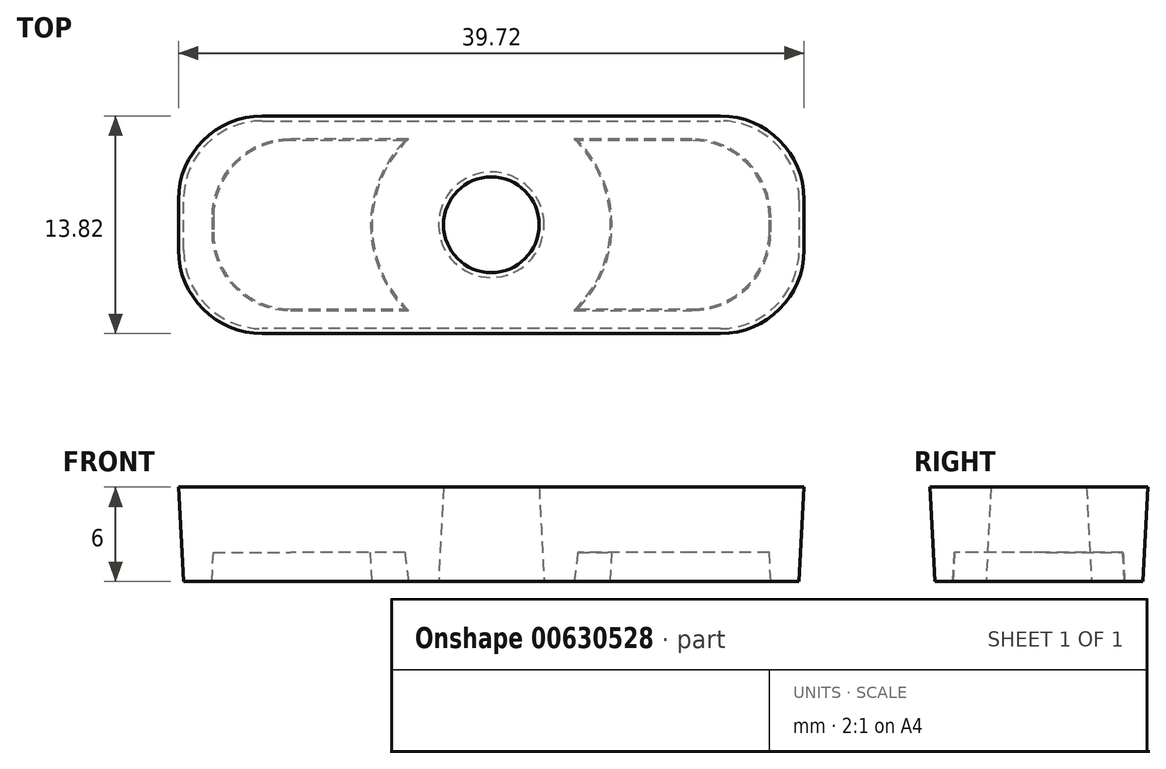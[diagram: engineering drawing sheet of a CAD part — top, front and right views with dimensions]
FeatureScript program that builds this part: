
annotation { "Feature Type Name" : "Feature", "Feature Type Description" : "" }
export const myFeature = defineFeature(function(context is Context, id is Id, definition is map)
    precondition{}
    {
        {
            var Q0;
            Q0=qCreatedBy(makeId("Top.planeOp"),FACE);
            var sketch = newSketch(context, id + "F0", { "sketchPlane" : qUnion([Q0])});
            skLineSegment(sketch, "E0.bottom", {"start": v(-12.75, 5.45) * mm, "end": v(12.75, 5.45) * mm});
            skLineSegment(sketch, "E0.top", {"start": v(-12.75, -5.45) * mm, "end": v(12.75, -5.45) * mm});
            skLineSegment(sketch, "E0.left", {"start": v(-17.75, 0.45) * mm, "end": v(-17.75, -0.45) * mm});
            skLineSegment(sketch, "E0.right", {"start": v(17.75, 0.45) * mm, "end": v(17.75, -0.45) * mm});
            skPoint(sketch, "E0.middle", {"position": v(0, 0) * mm});
            skArc(sketch, "E1", {"start": v(-5.26, 5.45) * mm, "mid": v(-7.58, 0) * mm, "end": v(-5.26, -5.45) * mm});
            skArc(sketch, "E2.trimOffspring", {"start": v(5.26, -5.45) * mm, "mid": v(7.58, 0) * mm, "end": v(5.26, 5.45) * mm});
            skCircle(sketch, "E3", {"center": v(0, 0) * mm, "radius": 3.35 * mm});
            skPoint(sketch, "E4.visualSharp", {"position": v(-17.75, 5.45) * mm});
            skArc(sketch, "E4.filletArc", {"start": v(-12.75, 5.45) * mm, "mid": v(-16.29, 3.99) * mm, "end": v(-17.75, 0.45) * mm});
            skPoint(sketch, "E5.visualSharp", {"position": v(-17.75, -5.45) * mm});
            skArc(sketch, "E5.filletArc", {"start": v(-17.75, -0.45) * mm, "mid": v(-16.29, -3.99) * mm, "end": v(-12.75, -5.45) * mm});
            skPoint(sketch, "E6.visualSharp", {"position": v(17.75, -5.45) * mm});
            skArc(sketch, "E6.filletArc", {"start": v(12.75, -5.45) * mm, "mid": v(16.29, -3.99) * mm, "end": v(17.75, -0.45) * mm});
            skPoint(sketch, "E7.visualSharp", {"position": v(17.75, 5.45) * mm});
            skArc(sketch, "E7.filletArc", {"start": v(17.75, 0.45) * mm, "mid": v(16.29, 3.99) * mm, "end": v(12.75, 5.45) * mm});
            skLineSegment(sketch, "E8.0", {"start": v(-14.55, 6.6) * mm, "end": v(12.75, 6.6) * mm});
            skLineSegment(sketch, "E9.0", {"start": v(-14.55, -6.6) * mm, "end": v(12.75, -6.6) * mm});
            skLineSegment(sketch, "E10.0", {"start": v(-19.55, 1.6) * mm, "end": v(-19.55, -1.6) * mm});
            skPoint(sketch, "E11.visualSharp", {"position": v(-19.55, 6.6) * mm});
            skArc(sketch, "E11.filletArc", {"start": v(-14.55, 6.6) * mm, "mid": v(-18.09, 5.14) * mm, "end": v(-19.55, 1.6) * mm});
            skPoint(sketch, "E12.visualSharp", {"position": v(-19.55, -6.6) * mm});
            skArc(sketch, "E12.filletArc", {"start": v(-19.55, -1.6) * mm, "mid": v(-18.09, -5.14) * mm, "end": v(-14.55, -6.6) * mm});
            skArc(sketch, "E13.MirrorCS", {"start": v(14.55, 6.6) * mm, "mid": v(18.09, 5.14) * mm, "end": v(19.55, 1.6) * mm});
            skLineSegment(sketch, "E14.MirrorCS", {"start": v(19.55, 1.6) * mm, "end": v(19.55, -1.6) * mm});
            skArc(sketch, "E15.MirrorCS", {"start": v(19.55, -1.6) * mm, "mid": v(18.09, -5.14) * mm, "end": v(14.55, -6.6) * mm});
            skLineSegment(sketch, "E16.MirrorCS", {"start": v(14.55, 6.6) * mm, "end": v(-12.75, 6.6) * mm});
            skLineSegment(sketch, "E17.MirrorCS", {"start": v(14.55, -6.6) * mm, "end": v(-12.75, -6.6) * mm});
            skSolve(sketch);
        }
        {
            var Q0;
            Q0=makeQuery(id+"F0.imprint","IMPRINT",FACE,{"disambiguationData":[TD([[makeQuery(id+"F0.imprint","IMPRINT",EDGE,{"derivedFrom":sQuery(id+"F0.wireOp",EDGE,"E0.left")}),-1.0]])]});
            var Q1;
            {var subQ0=sQuery(id+"F0.wireOp",EDGE,"E1");Q1=makeQuery(id+"F0.imprint","IMPRINT",FACE,{"disambiguationData":[TD([[makeQuery(id+"F0.imprint","IMPRINT",EDGE,{"derivedFrom":subQ0}),1.0]])]});}
            extrude(context, id + "F1", {"entities" : qUnion([Q0, Q1]), "depth" : 6 * mm, "offsetDistance" : 25 * mm, "hasDraft" : true, "draftAngle" : 3 * degree});
        }
        {
            var Q0;
            Q0=makeQuery(id+"F1.opExtrude","CAP_FACE",FACE,{"disambiguationData":[OSD([sQuery(id+"F0.wireOp",EDGE,"E0.bottom"),sQuery(id+"F0.wireOp",EDGE,"E0.top"),sQuery(id+"F0.wireOp",EDGE,"E0.left"),sQuery(id+"F0.wireOp",EDGE,"E0.right"),sQuery(id+"F0.wireOp",EDGE,"E1"),sQuery(id+"F0.wireOp",EDGE,"E2.trimOffspring"),sQuery(id+"F0.wireOp",EDGE,"E3"),sQuery(id+"F0.wireOp",EDGE,"E4.filletArc"),sQuery(id+"F0.wireOp",EDGE,"E5.filletArc"),sQuery(id+"F0.wireOp",EDGE,"E6.filletArc"),sQuery(id+"F0.wireOp",EDGE,"E7.filletArc"),sQuery(id+"F0.wireOp",EDGE,"E8.0"),sQuery(id+"F0.wireOp",EDGE,"E9.0"),sQuery(id+"F0.wireOp",EDGE,"E10.0"),sQuery(id+"F0.wireOp",EDGE,"E11.filletArc"),sQuery(id+"F0.wireOp",EDGE,"E12.filletArc"),sQuery(id+"F0.wireOp",EDGE,"E13.MirrorCS"),sQuery(id+"F0.wireOp",EDGE,"E14.MirrorCS"),sQuery(id+"F0.wireOp",EDGE,"E15.MirrorCS"),sQuery(id+"F0.wireOp",EDGE,"E16.MirrorCS"),sQuery(id+"F0.wireOp",EDGE,"E17.MirrorCS")])],"isStart":false});
            var sketch = newSketch(context, id + "F2", { "sketchPlane" : qUnion([Q0])});
            skLineSegment(sketch, "E18.0", {"start": v(-12.75, 5.14) * mm, "end": v(-5.99, 5.14) * mm});
            skArc(sketch, "E19.0", {"start": v(-12.75, 5.14) * mm, "mid": v(-16.06, 3.76) * mm, "end": v(-17.44, 0.45) * mm});
            skArc(sketch, "E20.0", {"start": v(-17.44, -0.45) * mm, "mid": v(-16.06, -3.76) * mm, "end": v(-12.75, -5.14) * mm});
            skPoint(sketch, "E21.0", {"position": v(-17.44, 0) * mm});
            skLineSegment(sketch, "E22.0", {"start": v(-17.44, 0.45) * mm, "end": v(-17.44, -0.45) * mm});
            skLineSegment(sketch, "E23.0", {"start": v(-12.75, -5.14) * mm, "end": v(-5.99, -5.14) * mm});
            skArc(sketch, "E24.0", {"start": v(-5.99, 5.14) * mm, "mid": v(-7.89, 0) * mm, "end": v(-5.99, -5.14) * mm});
            skArc(sketch, "E25.0", {"start": v(5.99, -5.14) * mm, "mid": v(7.89, 0) * mm, "end": v(5.99, 5.14) * mm});
            skLineSegment(sketch, "E26.0", {"start": v(5.99, 5.14) * mm, "end": v(12.75, 5.14) * mm});
            skArc(sketch, "E27.0", {"start": v(17.44, 0.45) * mm, "mid": v(16.06, 3.76) * mm, "end": v(12.75, 5.14) * mm});
            skLineSegment(sketch, "E28.0", {"start": v(17.44, 0.45) * mm, "end": v(17.44, -0.45) * mm});
            skArc(sketch, "E29.0", {"start": v(12.75, -5.14) * mm, "mid": v(16.06, -3.76) * mm, "end": v(17.44, -0.45) * mm});
            skLineSegment(sketch, "E30.0", {"start": v(5.99, -5.14) * mm, "end": v(12.75, -5.14) * mm});
            skLineSegment(sketch, "E31.0.0", {"start": v(-14.55, -6.91) * mm, "end": v(14.55, -6.91) * mm});
            skArc(sketch, "E31.0.1", {"start": v(19.86, -1.6) * mm, "mid": v(18.3, -5.36) * mm, "end": v(14.55, -6.91) * mm});
            skLineSegment(sketch, "E31.0.2", {"start": v(19.86, -1.6) * mm, "end": v(19.86, 1.6) * mm});
            skArc(sketch, "E31.0.3", {"start": v(14.55, 6.91) * mm, "mid": v(18.3, 5.36) * mm, "end": v(19.86, 1.6) * mm});
            skLineSegment(sketch, "E31.0.4", {"start": v(14.55, 6.91) * mm, "end": v(-14.55, 6.91) * mm});
            skArc(sketch, "E31.0.5", {"start": v(-14.55, 6.91) * mm, "mid": v(-18.3, 5.36) * mm, "end": v(-19.86, 1.6) * mm});
            skLineSegment(sketch, "E31.0.6", {"start": v(-19.86, 1.6) * mm, "end": v(-19.86, -1.6) * mm});
            skArc(sketch, "E31.0.7", {"start": v(-19.86, -1.6) * mm, "mid": v(-18.3, -5.36) * mm, "end": v(-14.55, -6.91) * mm});
            skSolve(sketch);
        }
        {
            var Q0;
            Q0=makeQuery(id+"F2.imprint","IMPRINT",FACE,{"disambiguationData":[TD([[makeQuery(id+"F2.imprint","IMPRINT",EDGE,{"derivedFrom":sQuery(id+"F2.wireOp",EDGE,"E18.0")}),-1.0]])]});
            var Q1;
            Q1=makeQuery(id+"F2.imprint","IMPRINT",FACE,{"disambiguationData":[TD([[makeQuery(id+"F2.imprint","IMPRINT",EDGE,{"derivedFrom":sQuery(id+"F2.wireOp",EDGE,"E25.0")}),-1.0]])]});
            var Q2;
            Q2=makeQuery(id+"F2.imprint","IMPRINT",FACE,{"disambiguationData":[TD([[makeQuery(id+"F2.imprint","IMPRINT",EDGE,{"derivedFrom":sQuery(id+"F2.wireOp",EDGE,"E18.0")}),1.0]])]});
            extrude(context, id + "F3", {"entities" : qUnion([Q0, Q1, Q2]), "operationType" : NewBodyOperationType.ADD, "oppositeDirection" : true, "depth" : (6 - 1.85) * mm, "offsetDistance" : 25 * mm, "hasDraft" : true, "draftAngle" : 3 * degree, "draftPullDirection" : true});
        }
    });
